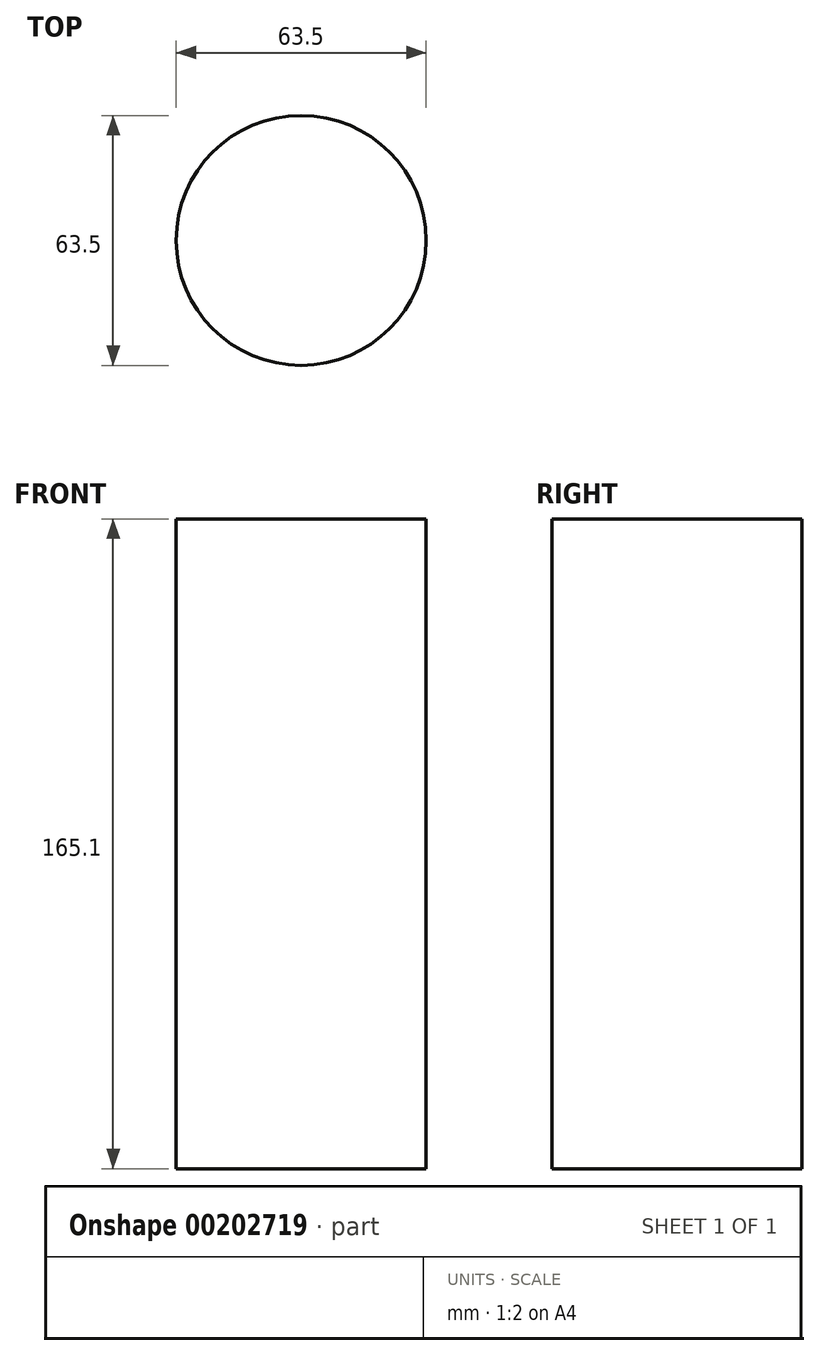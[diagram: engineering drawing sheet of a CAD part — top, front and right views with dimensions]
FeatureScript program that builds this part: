
annotation { "Feature Type Name" : "Feature", "Feature Type Description" : "" }
export const myFeature = defineFeature(function(context is Context, id is Id, definition is map)
    precondition{}
    {
        {
            var Q0;
            Q0=qCreatedBy(makeId("Top.planeOp"),FACE);
            var sketch = newSketch(context, id + "F0", { "sketchPlane" : qUnion([Q0])});
            skCircle(sketch, "E0", {"center": v(0, 0) * mm, "radius": 31.75 * mm});
            skSolve(sketch);
        }
        {
            var Q0;
            Q0=makeQuery(id+"F0.imprint","IMPRINT",FACE,{"disambiguationData":[TD([[makeQuery(id+"F0.imprint","IMPRINT",EDGE,{"derivedFrom":sQuery(id+"F0.wireOp",EDGE,"E0")}),1.0]])]});
            extrude(context, id + "F1", {"entities" : qUnion([Q0]), "depth" : 165.1 * mm});
        }
    });
